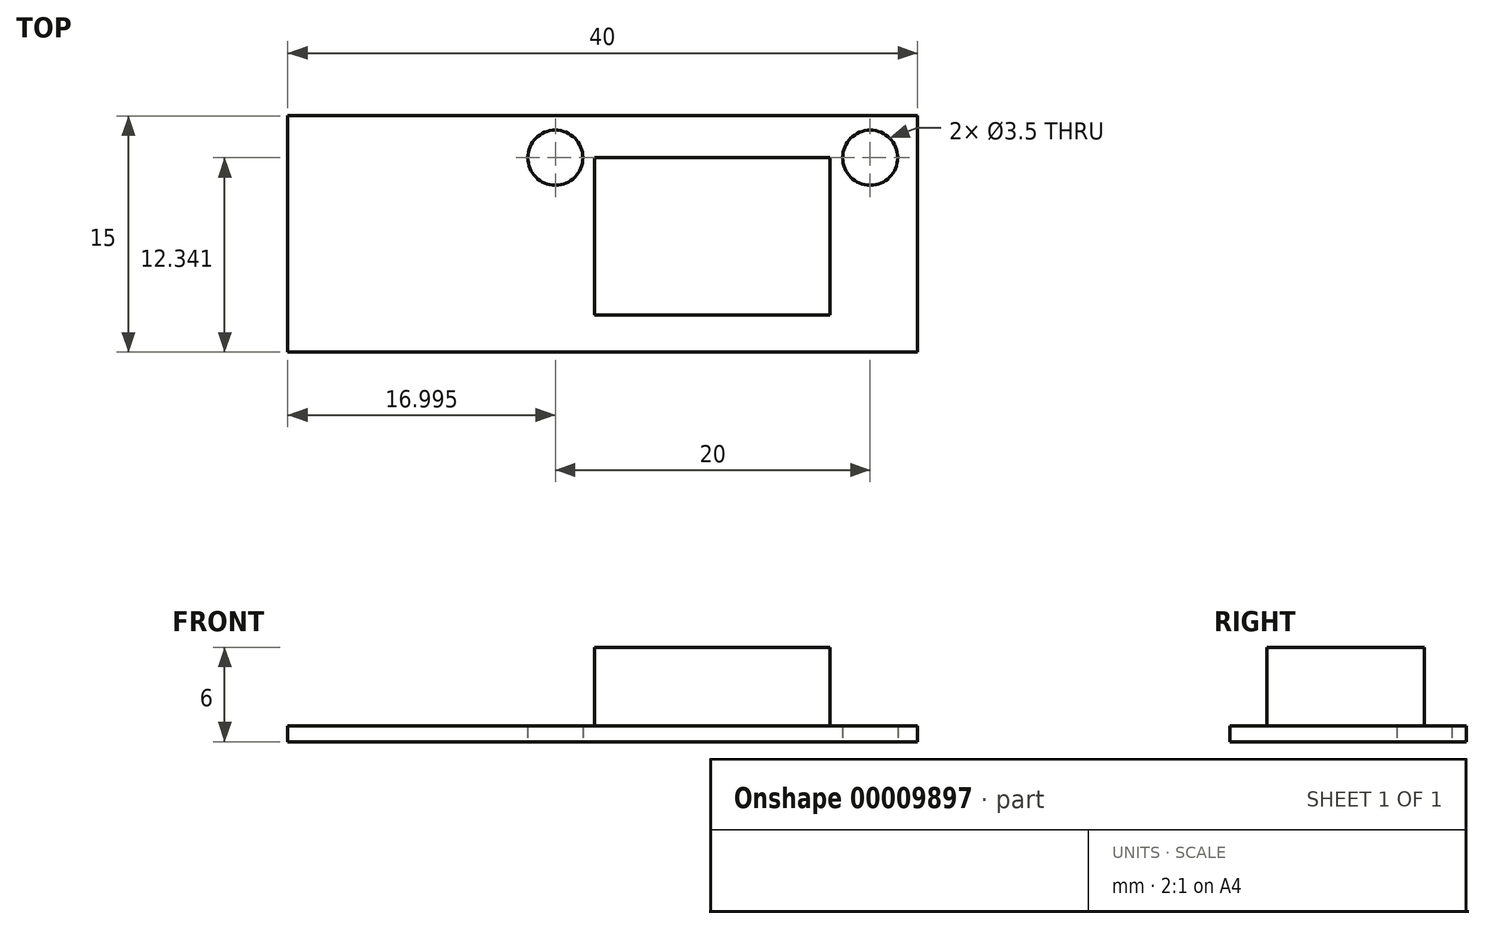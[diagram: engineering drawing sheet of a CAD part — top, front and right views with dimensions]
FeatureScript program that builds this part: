
annotation { "Feature Type Name" : "Feature", "Feature Type Description" : "" }
export const myFeature = defineFeature(function(context is Context, id is Id, definition is map)
    precondition{}
    {
        {
            var Q0;
            Q0=qCreatedBy(makeId("Top.planeOp"),FACE);
            var sketch = newSketch(context, id + "F0", { "sketchPlane" : qUnion([Q0])});
            skLineSegment(sketch, "E0.bottom", {"start": v(-16.63, 5.28) * mm, "end": v(23.37, 5.28) * mm});
            skLineSegment(sketch, "E0.top", {"start": v(-16.63, -9.72) * mm, "end": v(23.37, -9.72) * mm});
            skLineSegment(sketch, "E0.left", {"start": v(-16.63, 5.28) * mm, "end": v(-16.63, -9.72) * mm});
            skLineSegment(sketch, "E0.right", {"start": v(23.37, 5.28) * mm, "end": v(23.37, -9.72) * mm});
            skCircle(sketch, "E1", {"center": v(20.37, 2.62) * mm, "radius": 1.75 * mm});
            skCircle(sketch, "E2", {"center": v(0.37, 2.62) * mm, "radius": 1.75 * mm});
            skSolve(sketch);
        }
        {
            var Q0;
            Q0 = qSketchRegion(id + "F0", true);
            extrude(context, id + "F1", {"entities" : qUnion([Q0]), "depth" : 1 * mm});
        }
        {
            var Q0;
            Q0=makeQuery(id+"F1.opExtrude","CAP_FACE",FACE,{"disambiguationData":[OSD([sQuery(id+"F0.wireOp",EDGE,"E0.bottom"),sQuery(id+"F0.wireOp",EDGE,"E0.top"),sQuery(id+"F0.wireOp",EDGE,"E0.left"),sQuery(id+"F0.wireOp",EDGE,"E0.right"),sQuery(id+"F0.wireOp",EDGE,"E1"),sQuery(id+"F0.wireOp",EDGE,"E2")])],"isStart":false});
            var sketch = newSketch(context, id + "F2", { "sketchPlane" : qUnion([Q0])});
            skLineSegment(sketch, "E3.bottom", {"start": v(2.85, 2.65) * mm, "end": v(17.8, 2.65) * mm});
            skLineSegment(sketch, "E3.top", {"start": v(2.85, -7.38) * mm, "end": v(17.8, -7.38) * mm});
            skLineSegment(sketch, "E3.left", {"start": v(2.85, 2.65) * mm, "end": v(2.85, -7.38) * mm});
            skLineSegment(sketch, "E3.right", {"start": v(17.8, 2.65) * mm, "end": v(17.8, -7.38) * mm});
            skSolve(sketch);
        }
        {
            var Q0;
            Q0 = qSketchRegion(id + "F2", true);
            extrude(context, id + "F3", {"entities" : qUnion([Q0]), "operationType" : NewBodyOperationType.ADD, "depth" : 5 * mm});
        }
    });
